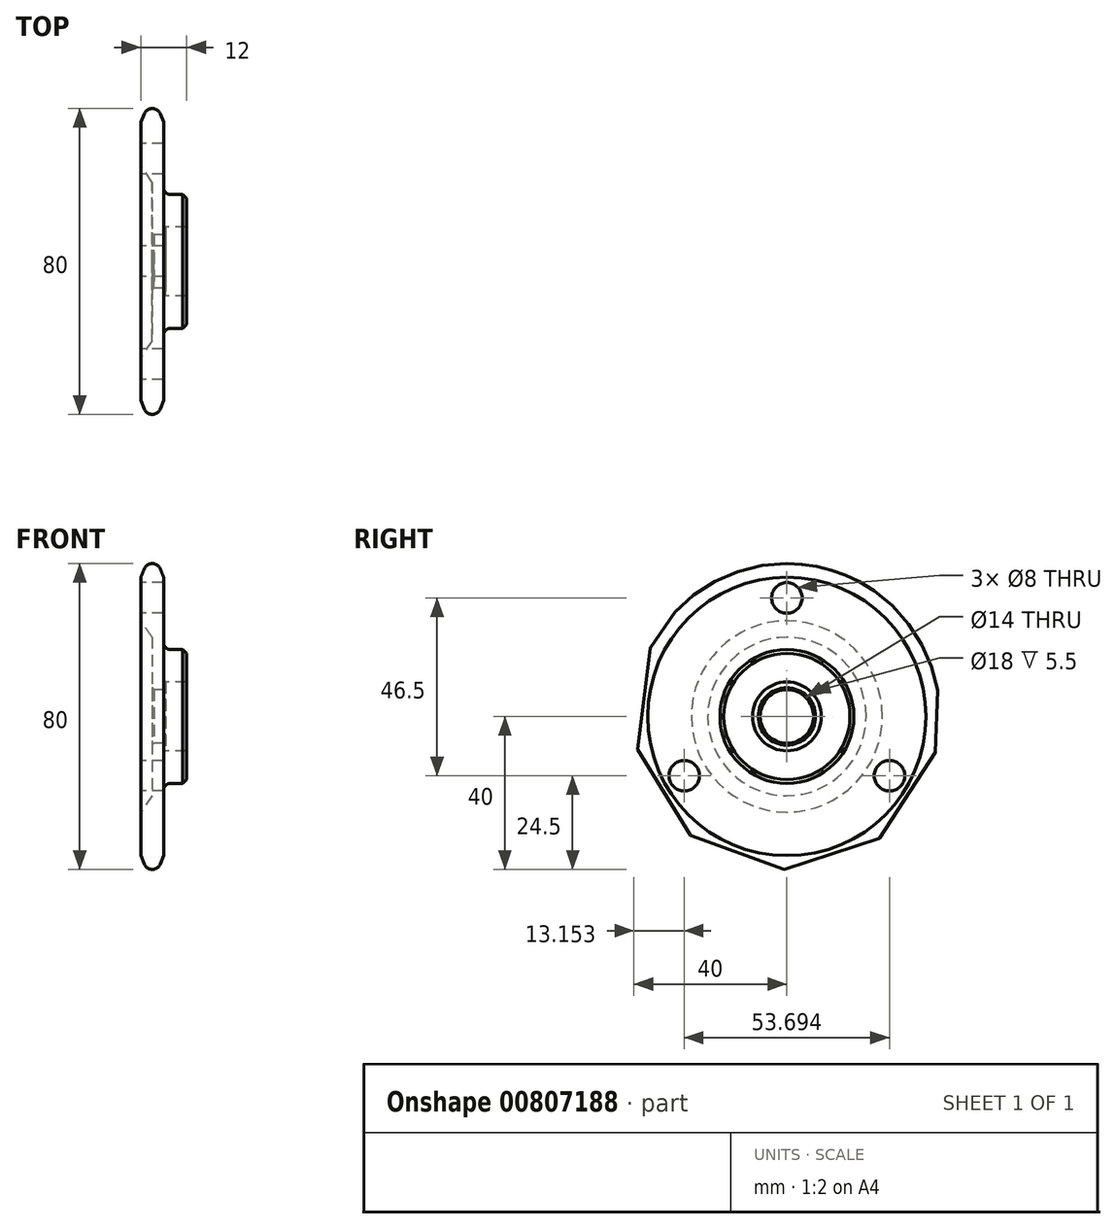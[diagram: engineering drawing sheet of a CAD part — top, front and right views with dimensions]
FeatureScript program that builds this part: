
annotation { "Feature Type Name" : "Feature", "Feature Type Description" : "" }
export const myFeature = defineFeature(function(context is Context, id is Id, definition is map)
    precondition{}
    {
        {
            var Q0;
            Q0=qCreatedBy(makeId("Front.planeOp"),FACE);
            var sketch = newSketch(context, id + "F0", { "sketchPlane" : qUnion([Q0])});
            skLineSegment(sketch, "E0", {"start": v(0, 25) * mm, "end": v(0, 36.39) * mm});
            skLineSegment(sketch, "E1", {"start": v(0, 36.39) * mm, "end": v(0.92, 38.61) * mm});
            skLineSegment(sketch, "E2", {"start": v(5.08, 38.61) * mm, "end": v(6, 36.39) * mm});
            skLineSegment(sketch, "E3", {"start": v(6, 36.39) * mm, "end": v(6, 17.5) * mm});
            skLineSegment(sketch, "E4", {"start": v(6, 17.5) * mm, "end": v(12, 17.5) * mm});
            skLineSegment(sketch, "E5", {"start": v(12, 17.5) * mm, "end": v(12, 9) * mm});
            skLineSegment(sketch, "E6", {"start": v(12, 9) * mm, "end": v(6.5, 9) * mm});
            skLineSegment(sketch, "E7", {"start": v(6.5, 9) * mm, "end": v(6.5, 7) * mm});
            skLineSegment(sketch, "E8", {"start": v(6.5, 7) * mm, "end": v(3, 7) * mm});
            skLineSegment(sketch, "E9", {"start": v(3, 7) * mm, "end": v(3, 20.72) * mm});
            skLineSegment(sketch, "E10", {"start": v(3, 20.72) * mm, "end": v(0, 25) * mm});
            skLineSegment(sketch, "E11", {"start": v(0, 36.39) * mm, "end": v(6, 36.39) * mm, "construction": true});
            skLineSegment(sketch, "E12", {"start": v(3, 36.39) * mm, "end": v(3, 48.1) * mm, "construction": true});
            skPoint(sketch, "E13.visualSharp", {"position": v(3, 43.63) * mm});
            skArc(sketch, "E13.filletArc", {"start": v(5.08, 38.61) * mm, "mid": v(3, 40) * mm, "end": v(0.92, 38.61) * mm});
            skLineSegment(sketch, "E14", {"start": v(0, 0) * mm, "end": v(22.68, 0) * mm, "construction": true});
            skSolve(sketch);
        }
        {
            var Q0;
            Q0 = qSketchRegion(id + "F0", true);
            var Q1;
            Q1=sQuery(id+"F0.wireOp",EDGE,"E14");
            revolve(context, id + "F1", {"surfaceOperationType" : NewSurfaceOperationType.NEW, "entities" : qUnion([Q0]), "axis" : qUnion([Q1]), "revolveType" : RevolveType.FULL});
        }
        {
            var Q0;
            Q0=makeQuery(id+"F1.opRevolve","SWEPT_EDGE",EDGE,{"disambiguationData":[OSD([sQuery(id+"F0.wireOp",EDGE,"E3"),sQuery(id+"F0.wireOp",EDGE,"E4")])]});
            fillet(context, id + "F2", {"entities" : qUnion([Q0]), "radius" : 1.75 * mm, "tangentPropagation" : true, "allowEdgeOverflow" : false});
        }
        {
            var Q0;
            Q0=makeQuery(id+"F1.opRevolve","SWEPT_EDGE",EDGE,{"disambiguationData":[OSD([sQuery(id+"F0.wireOp",EDGE,"E4"),sQuery(id+"F0.wireOp",EDGE,"E5")])]});
            chamfer(context, id + "F3", {"entities" : qUnion([Q0]), "width" : 1 * mm, "tangentPropagation" : true});
        }
        {
            var Q0;
            Q0=makeQuery(id+"F1.opRevolve","SWEPT_FACE",FACE,{"disambiguationData":[OSD([sQuery(id+"F0.wireOp",EDGE,"E0")])]});
            var sketch = newSketch(context, id + "F4", { "sketchPlane" : qUnion([Q0])});
            skCircle(sketch, "E15", {"center": v(0, 31) * mm, "radius": 4 * mm});
            skCircle(sketch, "E16.0", {"center": v(0, 0) * mm, "radius": 7 * mm, "construction": true});
            skCircle(sketch, "E17.1.0", {"center": v(-26.85, -15.5) * mm, "radius": 4 * mm});
            skCircle(sketch, "E17.2.0", {"center": v(26.85, -15.5) * mm, "radius": 4 * mm});
            skCircle(sketch, "E18", {"center": v(0, 0) * mm, "radius": 31 * mm, "construction": true});
            skSolve(sketch);
        }
        {
            var Q0;
            Q0 = qSketchRegion(id + "F4", true);
            extrude(context, id + "F5", {"entities" : qUnion([Q0]), "operationType" : NewBodyOperationType.REMOVE, "oppositeDirection" : true, "depth" : 25 * mm, "offsetDistance" : 25 * mm});
        }
        {
            var Q0;
            Q0=makeQuery(id+"F1.opRevolve","SWEPT_EDGE",EDGE,{"disambiguationData":[OSD([sQuery(id+"F0.wireOp",EDGE,"E7"),sQuery(id+"F0.wireOp",EDGE,"E8")])]});
            chamfer(context, id + "F6", {"entities" : qUnion([Q0]), "width" : 0.5 * mm, "tangentPropagation" : true});
        }
        {
            var Q0;
            Q0=makeQuery(id+"F1.opRevolve","SWEPT_EDGE",EDGE,{"disambiguationData":[OSD([sQuery(id+"F0.wireOp",EDGE,"E8"),sQuery(id+"F0.wireOp",EDGE,"E9")])]});
            chamfer(context, id + "F7", {"entities" : qUnion([Q0]), "width" : 0.5 * mm, "tangentPropagation" : true});
        }
    });
